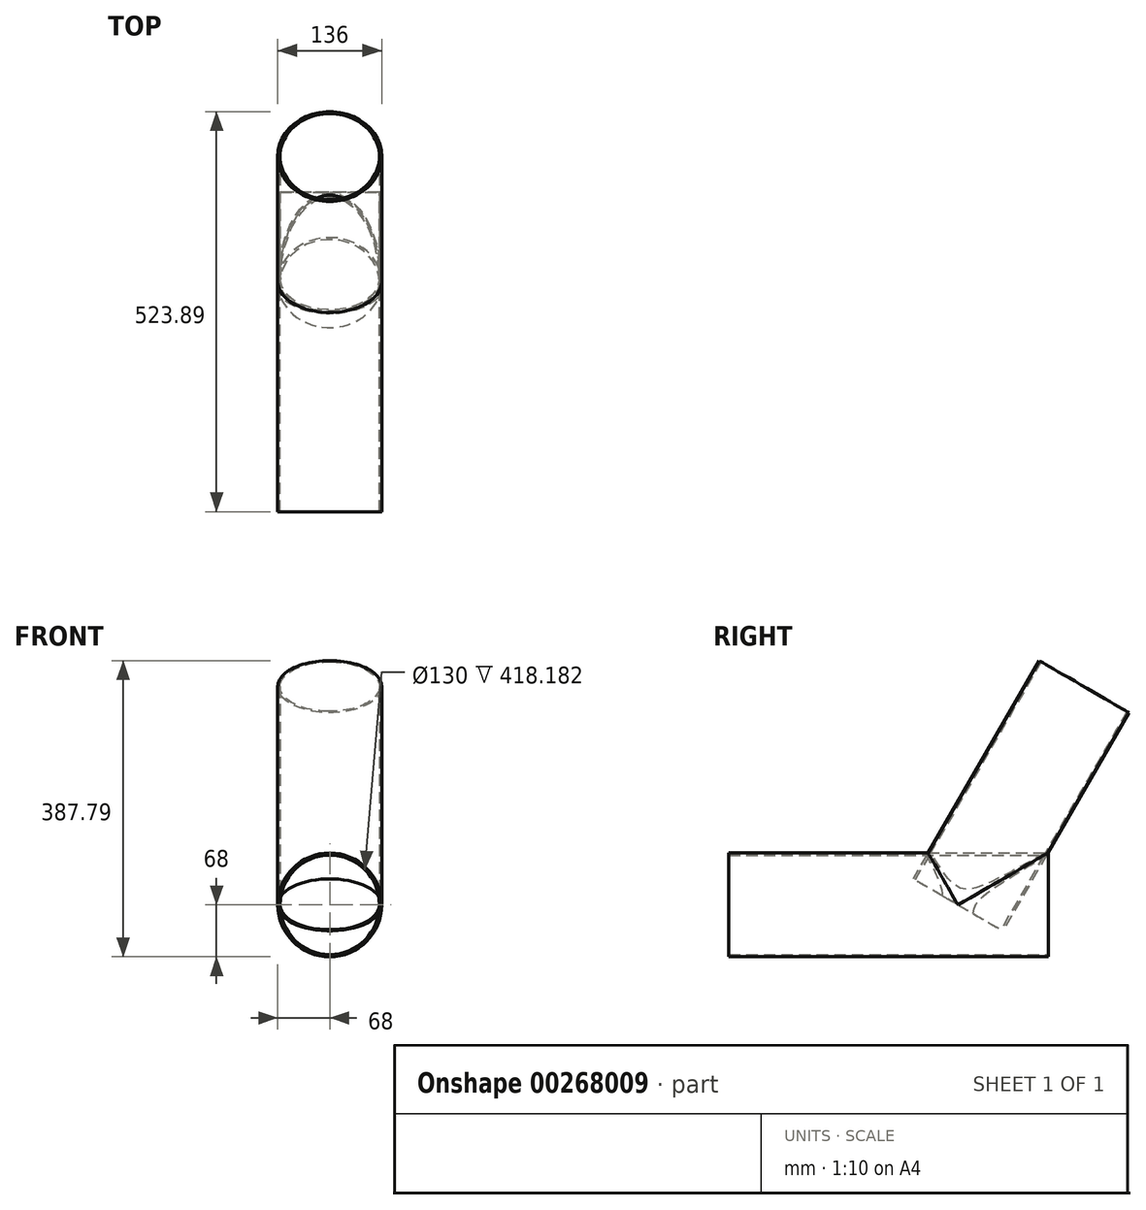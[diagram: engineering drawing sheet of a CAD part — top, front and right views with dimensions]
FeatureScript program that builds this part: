
annotation { "Feature Type Name" : "Feature", "Feature Type Description" : "" }
export const myFeature = defineFeature(function(context is Context, id is Id, definition is map)
    precondition{}
    {
        {
            assignVariable(context, id + "F0", {"variableType" : VariableType.LENGTH, "name" : "InternalDiam", "lengthValue" : 130 * mm});
        }
        {
            var Q0;
            Q0=qCreatedBy(makeId("Right.planeOp"),FACE);
            var sketch = newSketch(context, id + "F1", { "sketchPlane" : qUnion([Q0])});
            skLineSegment(sketch, "E0", {"start": v(0, 0) * mm, "end": v(-350, 0) * mm, "construction": true});
            skLineSegment(sketch, "E1", {"start": v(0, 0) * mm, "end": v(170.35, 295.05) * mm, "construction": true});
            skSolve(sketch);
        }
        {
            var Q0;
            Q0=sQuery(id+"F1.wireOp",EDGE,"E1");
            var Q1;
            Q1=sQuery(id+"F1.wireOp",VERTEX,"E0.start");
            cPlane(context, id + "F2", {"entities" : qUnion([Q0, Q1]), "cplaneType" : CPlaneType.LINE_POINT, "offset" : 25 * mm, "width" : 150 * mm, "height" : 150 * mm});
        }
        {
            var Q0;
            Q0=qCreatedBy(id+"F2.planeOp",FACE);
            var sketch = newSketch(context, id + "F3", { "sketchPlane" : qUnion([Q0])});
            skCircle(sketch, "E2", {"center": v(0, 0) * mm, "radius": 65 * mm});
            skCircle(sketch, "E3.0", {"center": v(0, 0) * mm, "radius": 68 * mm});
            skSolve(sketch);
        }
        {
            var Q0;
            Q0=makeQuery(id+"F3.imprint","IMPRINT",FACE,{"disambiguationData":[TD([[makeQuery(id+"F3.imprint","IMPRINT",EDGE,{"derivedFrom":sQuery(id+"F3.wireOp",EDGE,"E2")}),-1.0]])]});
            extrude(context, id + "F4", {"entities" : qUnion([Q0]), "depth" : 330 * mm, "offsetDistance" : 25 * mm});
        }
        {
            var Q0;
            Q0=qCreatedBy(makeId("Front.planeOp"),FACE);
            var sketch = newSketch(context, id + "F5", { "sketchPlane" : qUnion([Q0])});
            skCircle(sketch, "E4", {"center": v(0, 0) * mm, "radius": 65 * mm});
            skCircle(sketch, "E5.0", {"center": v(0, 0) * mm, "radius": 68 * mm});
            skSolve(sketch);
        }
        {
            var Q0;
            Q0=makeQuery(id+"F5.imprint","IMPRINT",FACE,{"disambiguationData":[TD([[makeQuery(id+"F5.imprint","IMPRINT",EDGE,{"derivedFrom":sQuery(id+"F5.wireOp",EDGE,"E4")}),-1.0]])]});
            extrude(context, id + "F6", {"entities" : qUnion([Q0]), "depth" : 300 * mm, "offsetDistance" : 25 * mm, "hasSecondDirection" : true, "secondDirectionOppositeDirection" : true, "secondDirectionDepth" : getVariable(context, 'InternalDiam') / 1.1});
        }
        {
            var Q0;
            Q0=makeQuery(id+"F6.opExtrude","SWEPT_BODY",BODY,{"disambiguationData":[OSD([sQuery(id+"F5.wireOp",EDGE,"E4"),sQuery(id+"F5.wireOp",EDGE,"E5.0")])]});
            var Q1;
            Q1=makeQuery(id+"F4.opExtrude","SWEPT_BODY",BODY,{"disambiguationData":[OSD([sQuery(id+"F3.wireOp",EDGE,"E2"),sQuery(id+"F3.wireOp",EDGE,"E3.0")])]});
            booleanBodies(context, id + "F7", {"operationType" : BooleanOperationType.SUBTRACTION, "tools" : qUnion([Q0]), "targets" : qUnion([Q1]), "keepTools" : true});
        }
    });
